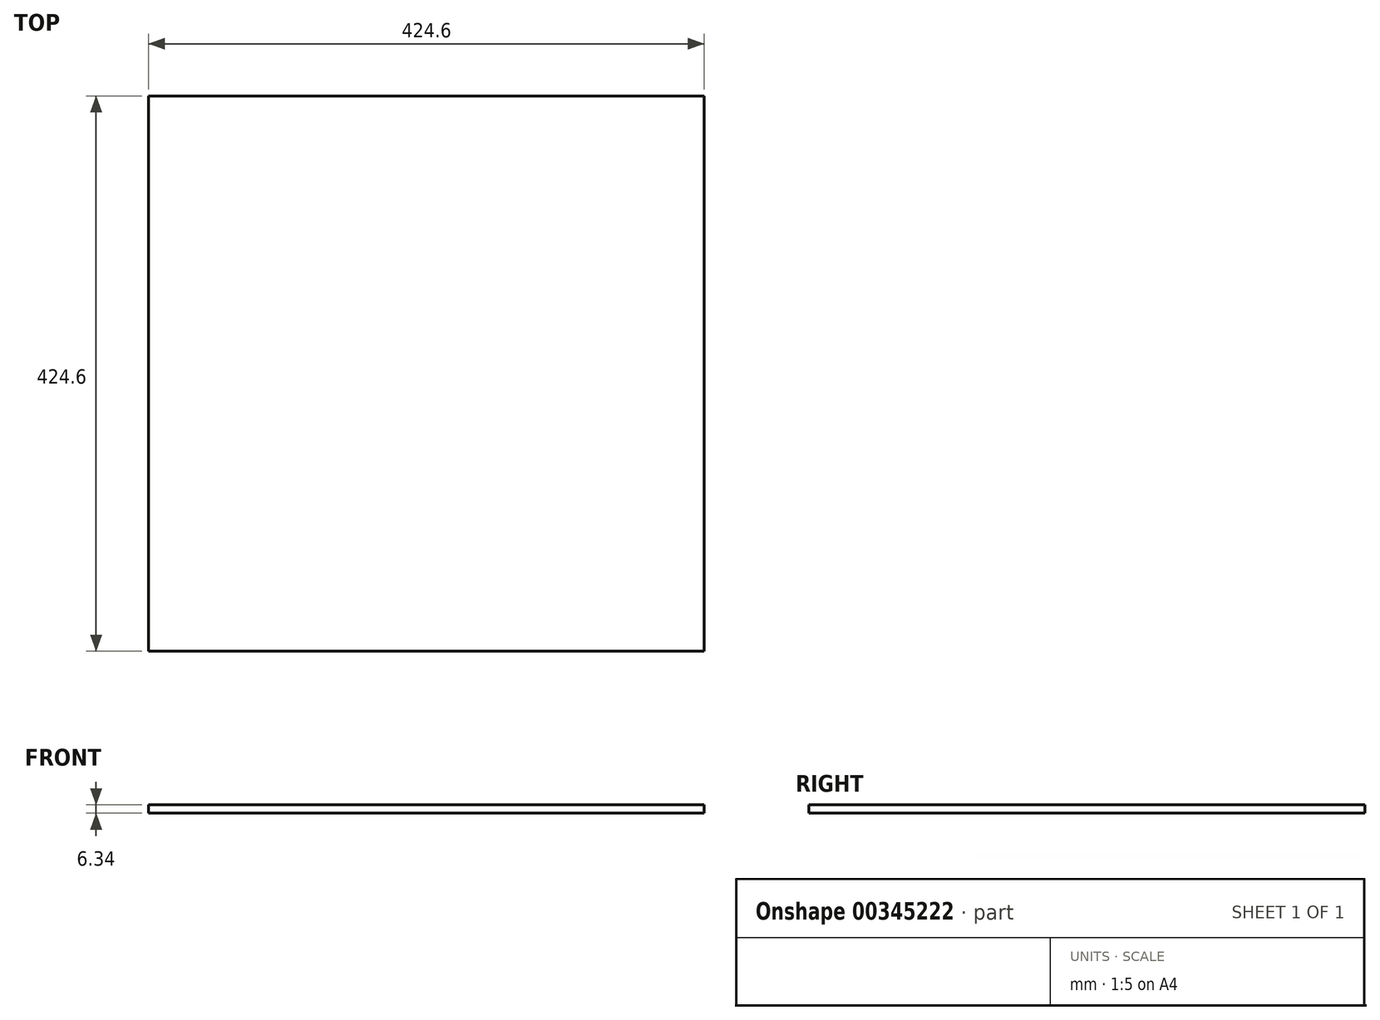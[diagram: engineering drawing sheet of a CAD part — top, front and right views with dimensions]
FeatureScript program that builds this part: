
annotation { "Feature Type Name" : "Feature", "Feature Type Description" : "" }
export const myFeature = defineFeature(function(context is Context, id is Id, definition is map)
    precondition{}
    {
        {
            var Q0;
            Q0=qCreatedBy(makeId("Top.planeOp"),FACE);
            var sketch = newSketch(context, id + "F0", { "sketchPlane" : qUnion([Q0])});
            skLineSegment(sketch, "E0.bottom", {"start": v(-212.3, 196.98) * mm, "end": v(212.3, 196.98) * mm});
            skLineSegment(sketch, "E0.top", {"start": v(-212.3, -227.62) * mm, "end": v(212.3, -227.62) * mm});
            skLineSegment(sketch, "E0.left", {"start": v(-212.3, 196.98) * mm, "end": v(-212.3, -227.62) * mm});
            skLineSegment(sketch, "E0.right", {"start": v(212.3, 196.98) * mm, "end": v(212.3, -227.62) * mm});
            skPoint(sketch, "E0.middle", {"position": v(0, -15.32) * mm});
            skSolve(sketch);
        }
        {
            var Q0;
            Q0=makeQuery(id+"F0.imprint","IMPRINT",FACE,{"disambiguationData":[TD([[makeQuery(id+"F0.imprint","IMPRINT",EDGE,{"derivedFrom":sQuery(id+"F0.wireOp",EDGE,"E0.bottom")}),-1.0]])]});
            extrude(context, id + "F1", {"entities" : qUnion([Q0]), "endBound" : BoundingType.SYMMETRIC, "depth" : 6.35 * mm});
        }
    });
